# Revit family: Kabelrinne SKS-SKS 130 FT,FS, TS SOK, FTSO
name_source: partatom
category: Generic Models
revit_build: Autodesk Revit 2017 (Build: 20160225_1515(x64)
units: mm (PartAtom-declared; Revit-internal decimal feet)

## family parameters
Always vertical = Yes
Can host rebar = No
Cut with Voids When Loaded = No
Part Type = Normal
Room Calculation Point = No
Round Connector Dimension = Use Diameter
Shared = No
Work Plane-Based = No

## types (4) — shared parameters
Cut's number = 2
Cut's number 2 = 60
Cut's number 3 = 59
Cut's number 4 = 4
Cut's space = 50 mm  [stored 0.164042 ft]
Height = 105 mm  [stored 0.344488 ft]
Length = 3000 mm  [stored 9.84252 ft]
Manufacturer = OBO Bettermann
URL = http://www.obo-bettermann.com
Width = 300 mm
Width 1 = 150 mm  [stored 0.492126 ft]
Width 2 = 150 mm  [stored 0.492126 ft]
Width/2 = 150 mm  [stored 0.492126 ft]

## per-type parameters (varying)
| type | GTIN | Manufacturer Art.No. | Material |
| SKS 130 FT | 4012196062652 | 6061656 | Hot-dip galvanised |
| SKS 130 FS | 4012196062294 | 6061303 | Strip-galvanised |
| SKS 130 FT SO | 4012196594993 | 7196025 | Hot-dip galvanised 85 µm |
| SKS 130 FTSoK | 4012196572458 | 7249903 | Hot-dip galvanised/special plastic-coated |

note: column(s) folded — value = type name in every type: Article Type

note: [stored X ft] marks values corroborated as IEEE doubles in the binary element streams (Revit-internal decimal feet)

## geometry (parser evidence)
native form markers: Sweep x3
no freeform markers — native parametric forms only
